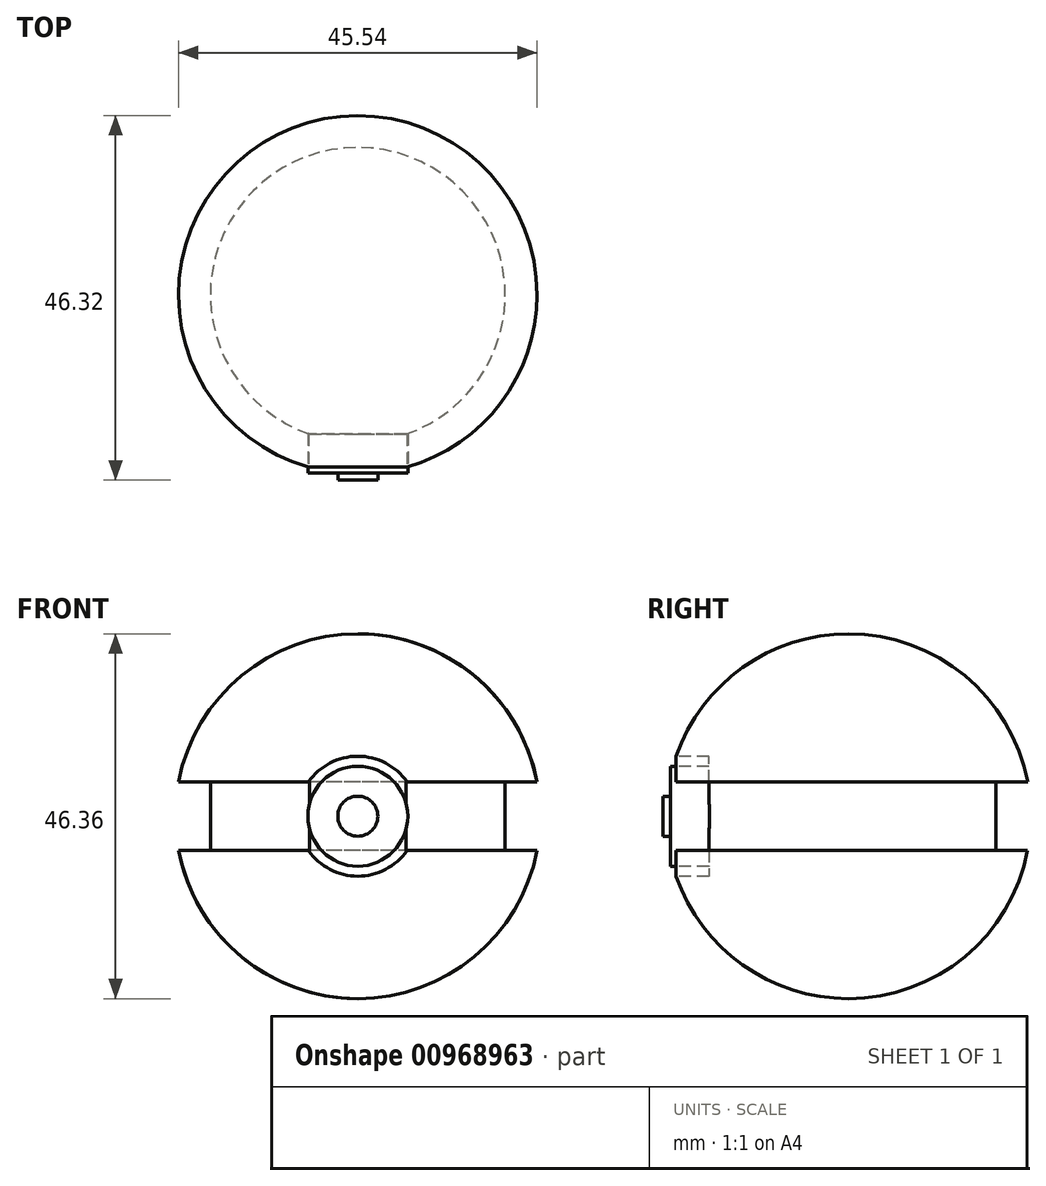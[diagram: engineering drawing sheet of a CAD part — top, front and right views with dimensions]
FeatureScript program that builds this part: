
annotation { "Feature Type Name" : "Feature", "Feature Type Description" : "" }
export const myFeature = defineFeature(function(context is Context, id is Id, definition is map)
    precondition{}
    {
        {
            var Q0;
            Q0=qCreatedBy(makeId("Front.planeOp"),FACE);
            var sketch = newSketch(context, id + "F0", { "sketchPlane" : qUnion([Q0])});
            skArc(sketch, "E0", {"start": v(-22.77, -4.36) * mm, "mid": v(-14.77, -17.86) * mm, "end": v(0, -23.18) * mm});
            skLineSegment(sketch, "E1", {"start": v(-22.77, 4.35) * mm, "end": v(-18.73, 4.35) * mm});
            skLineSegment(sketch, "E2", {"start": v(-18.73, 4.35) * mm, "end": v(-18.73, -4.36) * mm});
            skLineSegment(sketch, "E3", {"start": v(-18.73, -4.36) * mm, "end": v(-22.77, -4.36) * mm});
            skLineSegment(sketch, "E4", {"start": v(0, 23.18) * mm, "end": v(0, -23.18) * mm});
            skArc(sketch, "E5.trimOffspring", {"start": v(0, 23.18) * mm, "mid": v(-14.77, 17.86) * mm, "end": v(-22.77, 4.35) * mm});
            skSolve(sketch);
        }
        {
            var Q0;
            Q0 = qSketchRegion(id + "F0", true);
            var Q1;
            Q1=sQuery(id+"F0.wireOp",EDGE,"E4");
            revolve(context, id + "F1", {"surfaceOperationType" : NewSurfaceOperationType.NEW, "entities" : qUnion([Q0]), "axis" : qUnion([Q1]), "revolveType" : RevolveType.FULL});
        }
        {
            var Q0;
            Q0=qCreatedBy(makeId("Front.planeOp"),FACE);
            cPlane(context, id + "F2", {"entities" : qUnion([Q0]), "cplaneType" : CPlaneType.OFFSET, "offset" : 22.6 * mm, "width" : 152.4 * mm, "height" : 152.4 * mm});
        }
        {
            var Q0;
            Q0=qCreatedBy(id+"F2.planeOp",FACE);
            var sketch = newSketch(context, id + "F3", { "sketchPlane" : qUnion([Q0])});
            skCircle(sketch, "E6", {"center": v(0, 0) * mm, "radius": 7.62 * mm});
            skSolve(sketch);
        }
        {
            var Q0;
            Q0 = qSketchRegion(id + "F3", true);
            extrude(context, id + "F4", {"entities" : qUnion([Q0]), "operationType" : NewBodyOperationType.REMOVE, "depth" : 25.4 * mm, "offsetDistance" : 25.4 * mm});
        }
        {
            var Q0;
            Q0 = qSketchRegion(id + "F3", true);
            extrude(context, id + "F5", {"entities" : qUnion([Q0]), "operationType" : NewBodyOperationType.REMOVE, "oppositeDirection" : true, "depth" : 4.9 * mm, "offsetDistance" : 25.4 * mm});
        }
        {
            var Q0;
            Q0=qCreatedBy(id+"F2.planeOp",FACE);
            var sketch = newSketch(context, id + "F6", { "sketchPlane" : qUnion([Q0])});
            skCircle(sketch, "E7", {"center": v(0, 0) * mm, "radius": 6.35 * mm});
            skSolve(sketch);
        }
        {
            var Q0;
            Q0 = qSketchRegion(id + "F6", true);
            extrude(context, id + "F7", {"entities" : qUnion([Q0]), "operationType" : NewBodyOperationType.ADD, "oppositeDirection" : true, "depth" : 6.07 * mm, "offsetDistance" : 25.4 * mm});
        }
        {
            var Q0;
            Q0=qCreatedBy(id+"F2.planeOp",FACE);
            var sketch = newSketch(context, id + "F8", { "sketchPlane" : qUnion([Q0])});
            skCircle(sketch, "E8", {"center": v(0, 0) * mm, "radius": 2.54 * mm});
            skSolve(sketch);
        }
        {
            var Q0;
            Q0 = qSketchRegion(id + "F8", true);
            extrude(context, id + "F9", {"entities" : qUnion([Q0]), "operationType" : NewBodyOperationType.ADD, "depth" : 0.94 * mm, "offsetDistance" : 25.4 * mm});
        }
    });
